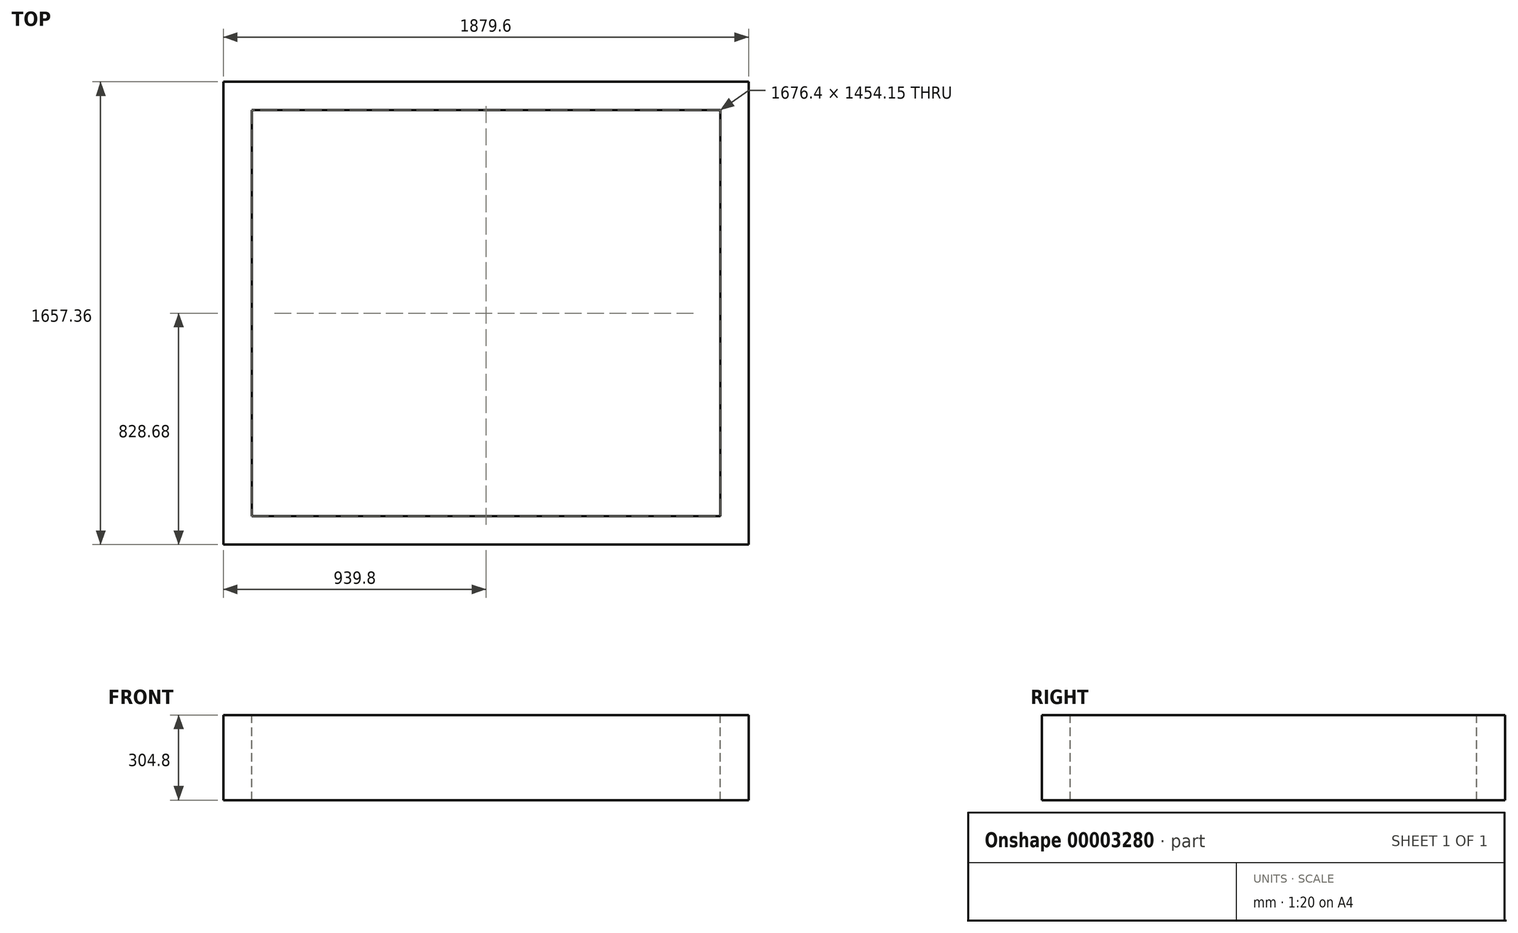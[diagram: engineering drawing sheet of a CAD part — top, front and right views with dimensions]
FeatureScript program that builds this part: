
annotation { "Feature Type Name" : "Feature", "Feature Type Description" : "" }
export const myFeature = defineFeature(function(context is Context, id is Id, definition is map)
    precondition{}
    {
        {
            var Q0;
            Q0=qCreatedBy(makeId("Top.planeOp"),FACE);
            var sketch = newSketch(context, id + "F0", { "sketchPlane" : qUnion([Q0])});
            skLineSegment(sketch, "E0.rect.bottom", {"start": v(838.2, -727.07) * mm, "end": v(-838.2, -727.08) * mm});
            skLineSegment(sketch, "E0.rect.top", {"start": v(838.2, 727.08) * mm, "end": v(-838.2, 727.07) * mm});
            skLineSegment(sketch, "E0.rect.left", {"start": v(838.2, -727.07) * mm, "end": v(838.2, 727.08) * mm});
            skLineSegment(sketch, "E0.rect.right", {"start": v(-838.2, -727.08) * mm, "end": v(-838.2, 727.07) * mm});
            skPoint(sketch, "E0.rect.middle", {"position": v(0, 0) * mm});
            skLineSegment(sketch, "E1.rect.bottom", {"start": v(-939.8, -828.68) * mm, "end": v(939.8, -828.68) * mm});
            skLineSegment(sketch, "E1.rect.top", {"start": v(-939.8, 828.68) * mm, "end": v(939.8, 828.68) * mm});
            skLineSegment(sketch, "E1.rect.left", {"start": v(-939.8, -828.68) * mm, "end": v(-939.8, 828.68) * mm});
            skLineSegment(sketch, "E1.rect.right", {"start": v(939.8, -828.68) * mm, "end": v(939.8, 828.68) * mm});
            skSolve(sketch);
        }
        {
            var Q0;
            Q0=makeQuery(id+"F0.imprint","IMPRINT",FACE,{"disambiguationData":[TD([[makeQuery(id+"F0.imprint","IMPRINT",EDGE,{"derivedFrom":sQuery(id+"F0.wireOp",EDGE,"E0.rect.bottom")}),1.0]])]});
            extrude(context, id + "F1", {"entities" : qUnion([Q0]), "oppositeDirection" : true, "depth" : 304.8 * mm});
        }
    });
